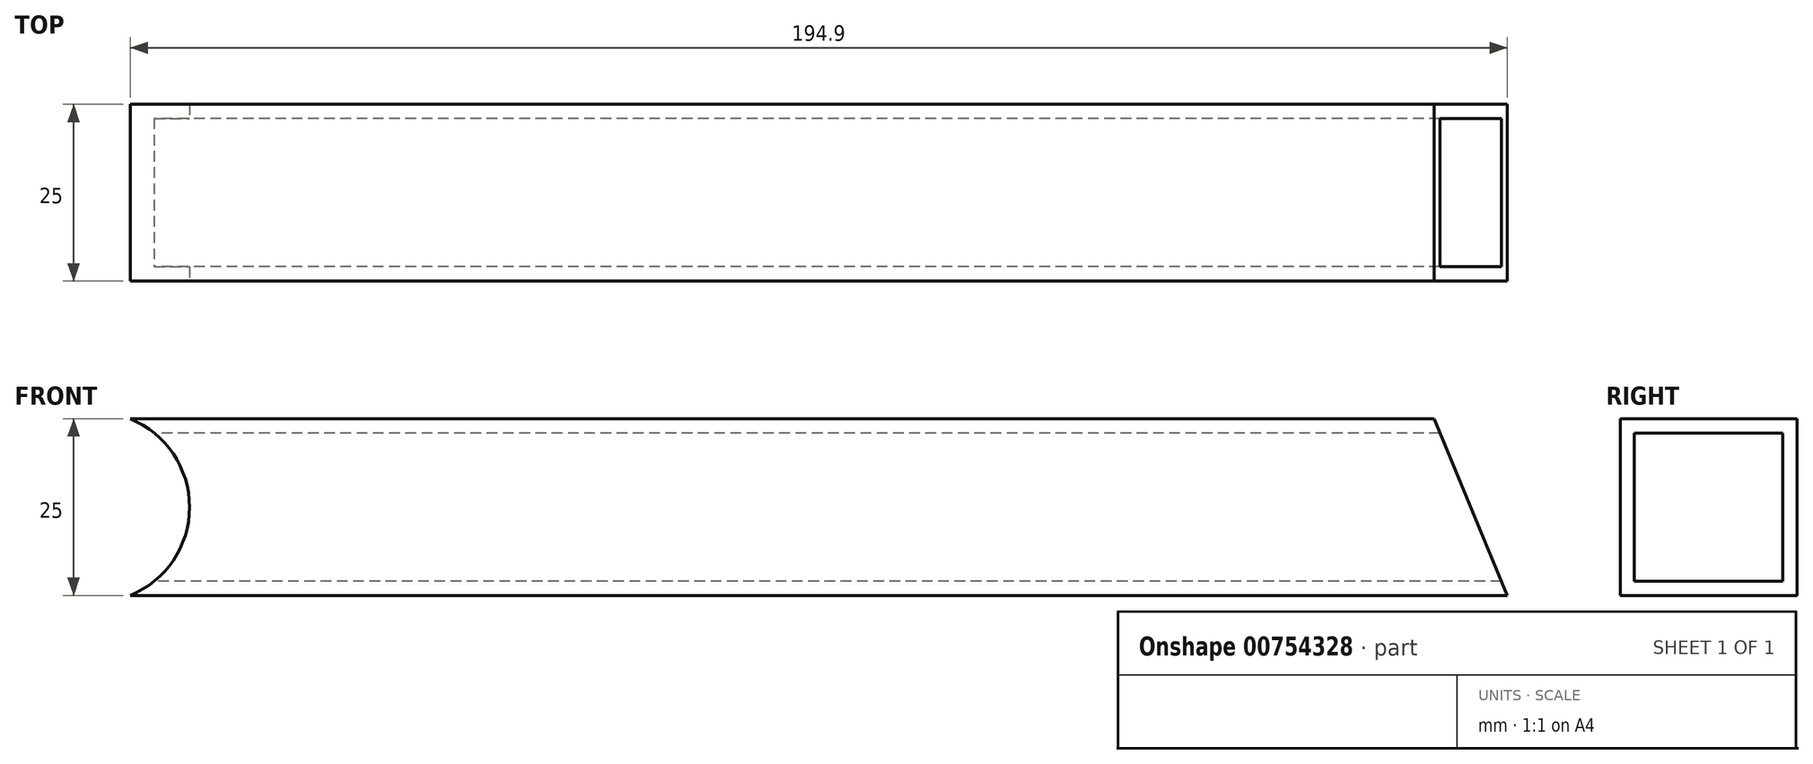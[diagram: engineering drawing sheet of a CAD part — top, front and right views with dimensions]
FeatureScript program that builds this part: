
annotation { "Feature Type Name" : "Feature", "Feature Type Description" : "" }
export const myFeature = defineFeature(function(context is Context, id is Id, definition is map)
    precondition{}
    {
        {
            var Q0;
            Q0=qCreatedBy(makeId("Right.planeOp"),FACE);
            var sketch = newSketch(context, id + "F0", { "sketchPlane" : qUnion([Q0])});
            skLineSegment(sketch, "E0.bottom", {"start": v(-12.5, 12.5) * mm, "end": v(12.5, 12.5) * mm});
            skLineSegment(sketch, "E0.top", {"start": v(-12.5, -12.5) * mm, "end": v(12.5, -12.5) * mm});
            skLineSegment(sketch, "E0.left", {"start": v(-12.5, 12.5) * mm, "end": v(-12.5, -12.5) * mm});
            skLineSegment(sketch, "E0.right", {"start": v(12.5, 12.5) * mm, "end": v(12.5, -12.5) * mm});
            skPoint(sketch, "E0.middle", {"position": v(0, 0) * mm});
            skLineSegment(sketch, "E1.bottom", {"start": v(-10.5, -10.5) * mm, "end": v(10.5, -10.5) * mm});
            skLineSegment(sketch, "E1.top", {"start": v(-10.5, 10.5) * mm, "end": v(10.5, 10.5) * mm});
            skLineSegment(sketch, "E1.left", {"start": v(-10.5, -10.5) * mm, "end": v(-10.5, 10.5) * mm});
            skLineSegment(sketch, "E1.right", {"start": v(10.5, -10.5) * mm, "end": v(10.5, 10.5) * mm});
            skLineSegment(sketch, "E2", {"start": v(-10.5, 10.5) * mm, "end": v(-12.5, 10.5) * mm, "construction": true});
            skLineSegment(sketch, "E3", {"start": v(-10.5, 10.5) * mm, "end": v(-10.5, 12.5) * mm, "construction": true});
            skSolve(sketch);
        }
        {
            var Q0;
            Q0 = qSketchRegion(id + "F0", true);
            extrude(context, id + "F1", {"entities" : qUnion([Q0]), "depth" : 200 * mm, "offsetDistance" : 25 * mm});
        }
        {
            var Q0;
            Q0=makeQuery(id+"F1.opExtrude","CAP_EDGE",EDGE,{"disambiguationData":[OSD([sQuery(id+"F0.wireOp",EDGE,"E0.bottom")])],"isStart":false});
            chamfer(context, id + "F2", {"entities" : qUnion([Q0]), "chamferType" : ChamferType.OFFSET_ANGLE, "width" : 25 * mm, "oppositeDirection" : true, "angle" : 22.5 * degree, "tangentPropagation" : true});
        }
        {
            var Q0;
            Q0=makeQuery(id+"F1.opExtrude","SWEPT_FACE",FACE,{"disambiguationData":[OSD([sQuery(id+"F0.wireOp",EDGE,"E0.left")])]});
            var sketch = newSketch(context, id + "F3", { "sketchPlane" : qUnion([Q0])});
            skCircle(sketch, "E4", {"center": v(0, 0) * mm, "radius": 13.5 * mm});
            skSolve(sketch);
        }
        {
            var Q0;
            Q0 = qSketchRegion(id + "F3", true);
            extrude(context, id + "F4", {"entities" : qUnion([Q0]), "operationType" : NewBodyOperationType.REMOVE, "oppositeDirection" : true, "depth" : 25 * mm, "offsetDistance" : 25 * mm});
        }
    });
